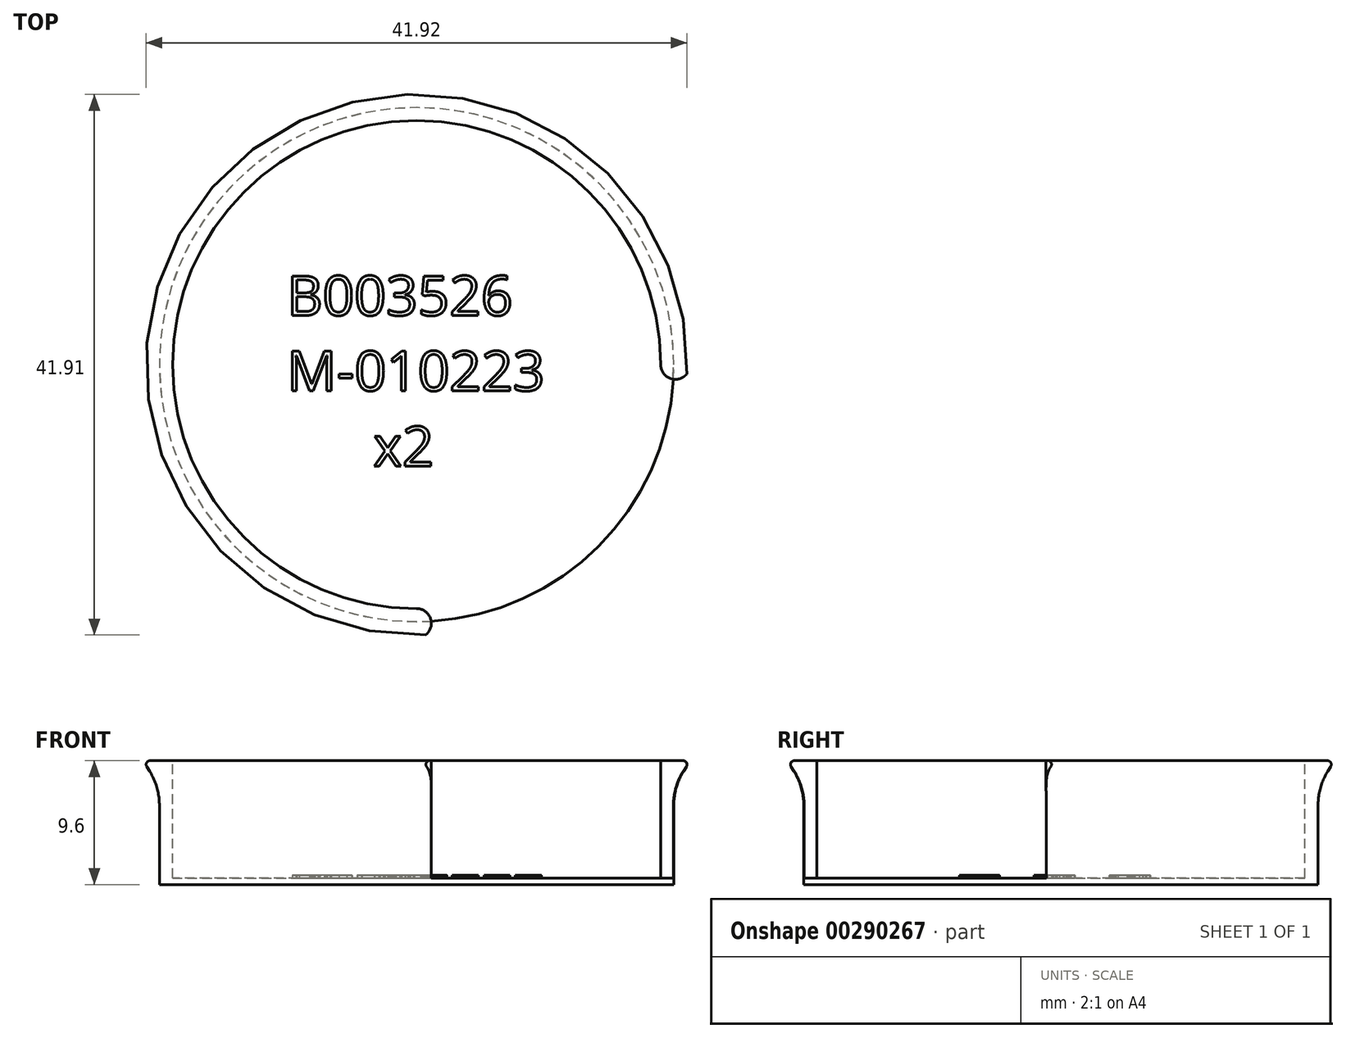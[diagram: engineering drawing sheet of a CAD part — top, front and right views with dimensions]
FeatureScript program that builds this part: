
annotation { "Feature Type Name" : "Feature", "Feature Type Description" : "" }
export const myFeature = defineFeature(function(context is Context, id is Id, definition is map)
    precondition{}
    {
        {
            var Q0;
            Q0=qCreatedBy(makeId("Right.planeOp"),FACE);
            var sketch = newSketch(context, id + "F0", { "sketchPlane" : qUnion([Q0])});
            skLineSegment(sketch, "E0", {"start": v(-36.1, 9.6) * mm, "end": v(-36.1, 0) * mm});
            skLineSegment(sketch, "E1", {"start": v(-36.1, 9.6) * mm, "end": v(-57.3, 9.6) * mm});
            skLineSegment(sketch, "E2", {"start": v(-36.1, 0) * mm, "end": v(-56.03, 0) * mm});
            skLineSegment(sketch, "E3", {"start": v(-56.03, 0) * mm, "end": v(-56.03, 7.57) * mm});
            skLineSegment(sketch, "E4", {"start": v(-56.03, 7.57) * mm, "end": v(-56.03, 9.6) * mm});
            skLineSegment(sketch, "E5", {"start": v(-57.3, 9.6) * mm, "end": v(-56.03, 7.57) * mm});
            skSolve(sketch);
        }
        {
            var Q0;
            Q0=qSketchRegion(id+"F0",true);
            var Q1;
            Q1=sQuery(id+"F0.wireOp",EDGE,"E0");
            revolve(context, id + "F1", {"entities" : qUnion([Q0]), "axis" : qUnion([Q1]), "revolveType" : RevolveType.FULL});
        }
        {
            var Q0;
            Q0=makeQuery(id+"F1.opRevolve","SWEPT_FACE",FACE,{"disambiguationData":[OSD([sQuery(id+"F0.wireOp",EDGE,"E1")])]});
            var sketch = newSketch(context, id + "F2", { "sketchPlane" : qUnion([Q0])});
            skCircle(sketch, "E6", {"center": v(0, -36.1) * mm, "radius": 18.91 * mm});
            skLineSegment(sketch, "E7.bottom", {"start": v(0, -36.1) * mm, "end": v(21.2, -36.1) * mm});
            skLineSegment(sketch, "E7.top", {"start": v(0, -57.3) * mm, "end": v(21.2, -57.3) * mm});
            skLineSegment(sketch, "E7.left", {"start": v(0, -36.1) * mm, "end": v(0, -57.3) * mm});
            skLineSegment(sketch, "E7.right", {"start": v(21.2, -36.1) * mm, "end": v(21.2, -57.3) * mm});
            skArc(sketch, "E8", {"start": v(0, -57.3) * mm, "mid": v(1.14, -56.15) * mm, "end": v(0, -55.01) * mm});
            skArc(sketch, "E9", {"start": v(18.91, -36.1) * mm, "mid": v(20.05, -37.24) * mm, "end": v(21.2, -36.1) * mm});
            skSolve(sketch);
        }
        {
            var Q0;
            {var subQ0=sQuery(id+"F2.wireOp",EDGE,"E7.left");var subQ3=sQuery(id+"F2.wireOp",EDGE,"E7.bottom");var subQ5=makeQuery(id+"F2.imprint","INTERSECT",VERTEX,{"derivedFrom":[subQ3,subQ0]});Q0=makeQuery(id+"F2.imprint","IMPRINT",FACE,{"disambiguationData":[TD([[makeQuery(id+"F2.imprint","IMPRINT",EDGE,{"disambiguationData":[TD([[subQ5,-1.0]])],"derivedFrom":subQ3}),1.0]])]});}
            var Q1;
            {var subQ0=sQuery(id+"F2.wireOp",EDGE,"E7.left");var subQ3=sQuery(id+"F2.wireOp",EDGE,"E7.bottom");var subQ5=makeQuery(id+"F2.imprint","INTERSECT",VERTEX,{"derivedFrom":[subQ3,subQ0]});Q1=makeQuery(id+"F2.imprint","IMPRINT",FACE,{"disambiguationData":[TD([[makeQuery(id+"F2.imprint","IMPRINT",EDGE,{"disambiguationData":[TD([[subQ5,-1.0]])],"derivedFrom":subQ3}),-1.0]])]});}
            var Q2;
            {var subQ0=sQuery(id+"F2.wireOp",EDGE,"E8");Q2=makeQuery(id+"F2.imprint","IMPRINT",FACE,{"disambiguationData":[TD([[makeQuery(id+"F2.imprint","IMPRINT",EDGE,{"derivedFrom":subQ0}),-1.0]])]});}
            extrude(context, id + "F3", {"entities" : qUnion([Q0, Q1, Q2]), "operationType" : NewBodyOperationType.REMOVE, "oppositeDirection" : true, "depth" : 9.1 * mm});
        }
        {
            var Q0;
            Q0=makeQuery(id+"F1.opRevolve","SWEPT_EDGE",EDGE,{"disambiguationData":[OSD([sQuery(id+"F0.wireOp",EDGE,"E1"),sQuery(id+"F0.wireOp",EDGE,"E5")])]});
            var Q1;
            Q1=makeQuery(id+"F3.boolean.opBoolean","COPY",EDGE,{"derivedFrom":makeQuery(id+"F3.opExtrude","CAP_EDGE",EDGE,{"disambiguationData":[OSD([sQuery(id+"F2.wireOp",EDGE,"E6")])],"isStart":true})});
            fillet(context, id + "F4", {"entities" : qUnion([Q0, Q1]), "radius" : 0.3 * mm, "tangentPropagation" : true, "allowEdgeOverflow" : false});
        }
        {
            var Q0;
            Q0=makeQuery(id+"F1.opRevolve","SWEPT_EDGE",EDGE,{"disambiguationData":[OSD([sQuery(id+"F0.wireOp",EDGE,"E3"),sQuery(id+"F0.wireOp",EDGE,"E4"),sQuery(id+"F0.wireOp",EDGE,"E5")])]});
            fillet(context, id + "F5", {"entities" : qUnion([Q0]), "radius" : 5 * mm, "tangentPropagation" : true, "allowEdgeOverflow" : false});
        }
        {
            var Q0;
            Q0=makeQuery(id+"F3.boolean.opBoolean","COPY",FACE,{"derivedFrom":makeQuery(id+"F3.opExtrude","CAP_FACE",FACE,{"disambiguationData":[OSD([sQuery(id+"F0.wireOp",EDGE,"E1"),sQuery(id+"F0.wireOp",EDGE,"E5"),sQuery(id+"F2.wireOp",EDGE,"E6"),sQuery(id+"F2.wireOp",EDGE,"E8"),sQuery(id+"F2.wireOp",EDGE,"E9")])],"isStart":false})});
            var sketch = newSketch(context, id + "F6", { "sketchPlane" : qUnion([Q0])});
            skText(sketch, "E10", { "text": "B003526\nM-010223\n      x2", "fontName": "OpenSans-Regular.ttf"});
            const initialGuessF6  = {"E10": [-0.01006, -0.03229, 1, 0, 0.00309]};
            skSetInitialGuess(sketch, initialGuessF6);
            skSolve(sketch);
        }
        {
            var Q0;
            Q0=qSketchRegion(id+"F6",true);
            extrude(context, id + "F7", {"entities" : qUnion([Q0]), "operationType" : NewBodyOperationType.ADD, "depth" : 0.2 * mm});
        }
    });
